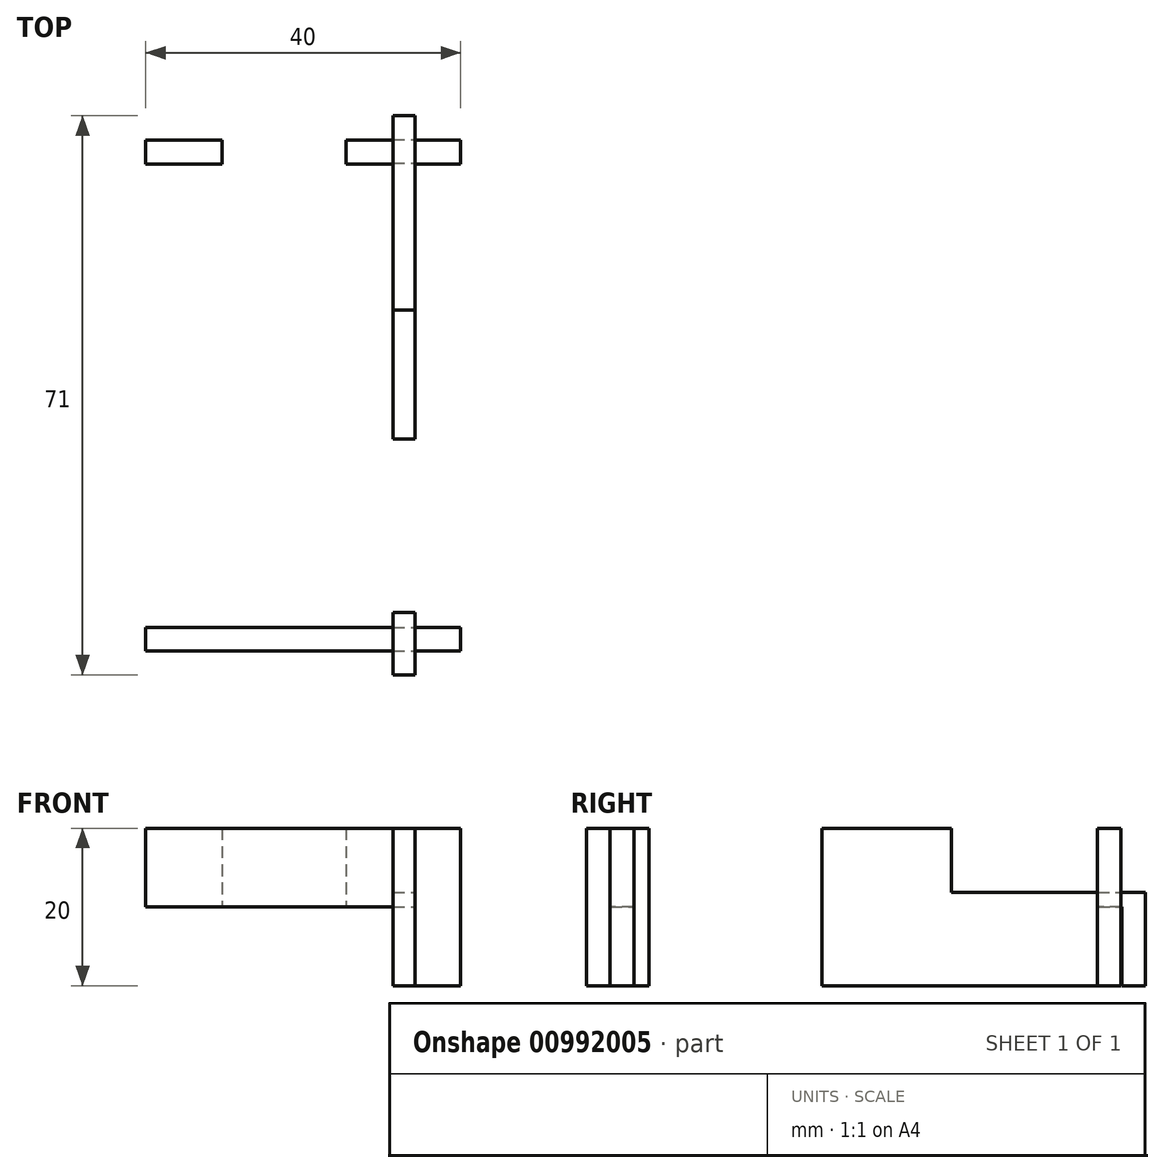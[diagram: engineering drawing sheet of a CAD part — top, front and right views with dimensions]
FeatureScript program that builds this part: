
annotation { "Feature Type Name" : "Feature", "Feature Type Description" : "" }
export const myFeature = defineFeature(function(context is Context, id is Id, definition is map)
    precondition{}
    {
        {
            var Q0;
            Q0=qCreatedBy(makeId("Front.planeOp"),FACE);
            var sketch = newSketch(context, id + "F0", { "sketchPlane" : qUnion([Q0])});
            skLineSegment(sketch, "E0.bottom", {"start": v(-40, 20) * mm, "end": v(0, 20) * mm});
            skLineSegment(sketch, "E0.top", {"start": v(-40, 0) * mm, "end": v(0, 0) * mm});
            skLineSegment(sketch, "E0.left", {"start": v(-40, 20) * mm, "end": v(-40, 0) * mm});
            skLineSegment(sketch, "E0.right", {"start": v(0, 20) * mm, "end": v(0, 0) * mm});
            skSolve(sketch);
        }
        {
            var Q0;
            Q0=makeQuery(id+"F0.imprint","IMPRINT",FACE,{"disambiguationData":[TD([[makeQuery(id+"F0.imprint","IMPRINT",EDGE,{"derivedFrom":sQuery(id+"F0.wireOp",EDGE,"E0.bottom")}),-1.0]])]});
            extrude(context, id + "F1", {"entities" : qUnion([Q0]), "depth" : 3 * mm, "offsetDistance" : 25 * mm});
        }
        {
            var Q0;
            Q0=makeQuery(id+"F1.opExtrude","SWEPT_FACE",FACE,{"disambiguationData":[OSD([sQuery(id+"F0.wireOp",EDGE,"E0.bottom")])]});
            var sketch = newSketch(context, id + "F2", { "sketchPlane" : qUnion([Q0])});
            skLineSegment(sketch, "E1.bottom", {"start": v(-8.59, 0) * mm, "end": v(-5.79, 0) * mm});
            skLineSegment(sketch, "E1.top", {"start": v(-8.59, -3) * mm, "end": v(-5.79, -3) * mm});
            skLineSegment(sketch, "E1.left", {"start": v(-8.59, 0) * mm, "end": v(-8.59, -3) * mm});
            skLineSegment(sketch, "E1.right", {"start": v(-5.79, 0) * mm, "end": v(-5.79, -3) * mm});
            skSolve(sketch);
        }
        {
            var Q0;
            Q0=makeQuery(id+"F2.imprint","IMPRINT",FACE,{"disambiguationData":[TD([[makeQuery(id+"F2.imprint","IMPRINT",EDGE,{"derivedFrom":sQuery(id+"F2.wireOp",EDGE,"E1.bottom")}),-1.0]])]});
            extrude(context, id + "F3", {"entities" : qUnion([Q0]), "operationType" : NewBodyOperationType.REMOVE, "oppositeDirection" : true, "depth" : 10 * mm, "offsetDistance" : 25 * mm});
        }
        {
            var Q0;
            {var subQ1=sQuery(id+"F0.wireOp",EDGE,"E0.left");var subQ3=sQuery(id+"F0.wireOp",EDGE,"E0.bottom");Q0=makeQuery(id+"F3.boolean.opBoolean","SPLIT",FACE,{"disambiguationData":[TD([makeQuery(id+"F1.opExtrude","SWEPT_FACE",FACE,{"disambiguationData":[OSD([subQ1])]})])],"derivedFrom":makeQuery(id+"F1.opExtrude","SWEPT_FACE",FACE,{"disambiguationData":[OSD([subQ3])]})});}
            var sketch = newSketch(context, id + "F4", { "sketchPlane" : qUnion([Q0])});
            skLineSegment(sketch, "E2", {"start": v(-8.59, 65) * mm, "end": v(-8.59, -6) * mm});
            skLineSegment(sketch, "E3", {"start": v(-8.59, -6) * mm, "end": v(-5.79, -6) * mm});
            skLineSegment(sketch, "E4", {"start": v(-5.79, -6) * mm, "end": v(-5.79, 65) * mm});
            skLineSegment(sketch, "E5", {"start": v(-5.79, 65) * mm, "end": v(-8.59, 65) * mm});
            skLineSegment(sketch, "E6", {"start": v(-14.6, 0) * mm, "end": v(-14.6, 59) * mm, "construction": true});
            skLineSegment(sketch, "E7", {"start": v(-14.6, 29.5) * mm, "end": v(-27.72, 29.5) * mm, "construction": true});
            skLineSegment(sketch, "E8", {"start": v(-8.59, 62) * mm, "end": v(-5.79, 62) * mm, "construction": true});
            skLineSegment(sketch, "E9", {"start": v(-8.59, -3) * mm, "end": v(-5.79, -3) * mm, "construction": true});
            skLineSegment(sketch, "E10", {"start": v(-7.19, -3) * mm, "end": v(-7.19, 62) * mm, "construction": true});
            skSolve(sketch);
        }
        {
            var Q0;
            {var subQ0=sQuery(id+"F4.wireOp",EDGE,"E3");Q0=makeQuery(id+"F4.imprint","IMPRINT",FACE,{"disambiguationData":[TD([[makeQuery(id+"F4.imprint","IMPRINT",EDGE,{"derivedFrom":subQ0}),1.0]])]});}
            var Q1;
            Q1=makeQuery(id+"F1.opExtrude","SWEPT_FACE",FACE,{"disambiguationData":[OSD([sQuery(id+"F0.wireOp",EDGE,"E0.top")])]});
            extrude(context, id + "F5", {"entities" : qUnion([Q0]), "endBound" : BoundingType.UP_TO_SURFACE, "oppositeDirection" : true, "depth" : 25 * mm, "endBoundEntityFace" : qUnion([Q1]), "offsetDistance" : 25 * mm});
        }
        {
            var Q0;
            {var subQ0=sQuery(id+"F4.wireOp",EDGE,"E5");var subQ1=sQuery(id+"F4.wireOp",EDGE,"E4");Q0=makeQuery(id+"F5.boolean.opBoolean","SPLIT",FACE,{"disambiguationData":[TD([makeQuery(id+"F5.opExtrude","SWEPT_FACE",FACE,{"disambiguationData":[OSD([subQ0])]})])],"derivedFrom":makeQuery(id+"F5.opExtrude","SWEPT_FACE",FACE,{"disambiguationData":[OSD([subQ1])]})});}
            var sketch = newSketch(context, id + "F6", { "sketchPlane" : qUnion([Q0])});
            skLineSegment(sketch, "E11", {"start": v(-3, 10) * mm, "end": v(-3, 0) * mm});
            skLineSegment(sketch, "E12", {"start": v(-3, 0) * mm, "end": v(0, 0) * mm});
            skLineSegment(sketch, "E13", {"start": v(0, 0) * mm, "end": v(0, 10) * mm});
            skLineSegment(sketch, "E14", {"start": v(0, 10) * mm, "end": v(-3, 10) * mm});
            skLineSegment(sketch, "E15.0", {"start": v(-6, 20) * mm, "end": v(65, 20) * mm, "construction": true});
            skLineSegment(sketch, "E16", {"start": v(29.5, 20) * mm, "end": v(29.5, -9.87) * mm, "construction": true});
            skLineSegment(sketch, "E17.MirrorCS", {"start": v(59, 10) * mm, "end": v(62, 10) * mm});
            skLineSegment(sketch, "E18.MirrorCS", {"start": v(59, 0) * mm, "end": v(59, 10) * mm});
            skLineSegment(sketch, "E19.MirrorCS", {"start": v(62, 10) * mm, "end": v(62, 0) * mm});
            skLineSegment(sketch, "E20.MirrorCS", {"start": v(62, 0) * mm, "end": v(59, 0) * mm});
            skSolve(sketch);
        }
        {
            var Q0;
            Q0 = qSketchRegion(id + "F6", true);
            extrude(context, id + "F7", {"entities" : qUnion([Q0]), "operationType" : NewBodyOperationType.REMOVE, "endBound" : BoundingType.THROUGH_ALL, "oppositeDirection" : true, "depth" : 25 * mm, "offsetDistance" : 25 * mm});
        }
        {
            var Q0;
            Q0=makeQuery(id+"F5.opExtrude","SWEPT_FACE",FACE,{"disambiguationData":[OSD([sQuery(id+"F4.wireOp",EDGE,"E4")])]});
            var sketch = newSketch(context, id + "F8", { "sketchPlane" : qUnion([Q0])});
            skLineSegment(sketch, "E21.bottom", {"start": v(1.92, 20) * mm, "end": v(23.92, 20) * mm});
            skLineSegment(sketch, "E21.top", {"start": v(1.92, 0) * mm, "end": v(23.92, 0) * mm});
            skLineSegment(sketch, "E21.left", {"start": v(1.92, 20) * mm, "end": v(1.92, 0) * mm});
            skLineSegment(sketch, "E21.right", {"start": v(23.92, 20) * mm, "end": v(23.92, 0) * mm});
            skSolve(sketch);
        }
        {
            var Q0;
            Q0=makeQuery(id+"F8.imprint","IMPRINT",FACE,{"disambiguationData":[TD([[makeQuery(id+"F8.imprint","IMPRINT",EDGE,{"derivedFrom":sQuery(id+"F8.wireOp",EDGE,"E21.bottom")}),-1.0]])]});
            extrude(context, id + "F9", {"entities" : qUnion([Q0]), "operationType" : NewBodyOperationType.REMOVE, "oppositeDirection" : true, "depth" : 25 * mm, "offsetDistance" : 25 * mm});
        }
        {
            var Q0;
            {var subQ0=sQuery(id+"F4.wireOp",EDGE,"E5");var subQ1=sQuery(id+"F4.wireOp",EDGE,"E4");Q0=makeQuery(id+"F9.boolean.opBoolean","SPLIT",FACE,{"disambiguationData":[TD([makeQuery(id+"F5.opExtrude","SWEPT_FACE",FACE,{"disambiguationData":[OSD([subQ0])]})])],"derivedFrom":makeQuery(id+"F5.opExtrude","SWEPT_FACE",FACE,{"disambiguationData":[OSD([subQ1])]})});}
            var sketch = newSketch(context, id + "F10", { "sketchPlane" : qUnion([Q0])});
            skLineSegment(sketch, "E22", {"start": v(40.33, 20) * mm, "end": v(40.33, 11.87) * mm});
            skLineSegment(sketch, "E23", {"start": v(40.33, 11.87) * mm, "end": v(65, 11.87) * mm});
            skLineSegment(sketch, "E24", {"start": v(40.33, 20) * mm, "end": v(65, 20) * mm});
            skLineSegment(sketch, "E25", {"start": v(65, 20) * mm, "end": v(65, 11.87) * mm});
            skSolve(sketch);
        }
        {
            var Q0;
            Q0=makeQuery(id+"F10.imprint","IMPRINT",FACE,{"disambiguationData":[TD([[makeQuery(id+"F10.imprint","IMPRINT",EDGE,{"derivedFrom":sQuery(id+"F10.wireOp",EDGE,"E22")}),1.0]])]});
            extrude(context, id + "F11", {"entities" : qUnion([Q0]), "operationType" : NewBodyOperationType.REMOVE, "oppositeDirection" : true, "depth" : 25 * mm, "offsetDistance" : 25 * mm});
        }
        {
            var Q0;
            Q0=makeQuery(id+"F1.opExtrude","SWEPT_BODY",BODY,{"disambiguationData":[OSD([sQuery(id+"F0.wireOp",EDGE,"E0.bottom"),sQuery(id+"F0.wireOp",EDGE,"E0.top"),sQuery(id+"F0.wireOp",EDGE,"E0.left"),sQuery(id+"F0.wireOp",EDGE,"E0.right")])]});
            transform(context, id + "F12", {"entities" : qUnion([Q0]), "transformType" : TransformType.TRANSLATION_3D, "dx" : 0 * mm, "dy" : 61.9 * mm, "dz" : 0 * mm, "makeCopy" : true});
        }
        {
            var Q0;
            Q0=makeQuery(id+"F12.opPattern","COPY",FACE,{"derivedFrom":makeQuery(id+"F1.opExtrude","CAP_FACE",FACE,{"disambiguationData":[OSD([sQuery(id+"F0.wireOp",EDGE,"E0.bottom"),sQuery(id+"F0.wireOp",EDGE,"E0.top"),sQuery(id+"F0.wireOp",EDGE,"E0.left"),sQuery(id+"F0.wireOp",EDGE,"E0.right")])],"isStart":true}),"instanceName":"1"});
            var sketch = newSketch(context, id + "F13", { "sketchPlane" : qUnion([Q0])});
            skLineSegment(sketch, "E26", {"start": v(14.56, 20) * mm, "end": v(14.56, 8.14) * mm});
            skLineSegment(sketch, "E27", {"start": v(14.56, 8.14) * mm, "end": v(30.32, 8.14) * mm});
            skLineSegment(sketch, "E28", {"start": v(30.32, 8.14) * mm, "end": v(30.32, 20) * mm});
            skLineSegment(sketch, "E29", {"start": v(30.32, 20) * mm, "end": v(14.56, 20) * mm});
            skSolve(sketch);
        }
        {
            var Q0;
            Q0=makeQuery(id+"F13.imprint","IMPRINT",FACE,{"disambiguationData":[TD([[makeQuery(id+"F13.imprint","IMPRINT",EDGE,{"derivedFrom":sQuery(id+"F13.wireOp",EDGE,"E26")}),1.0]])]});
            extrude(context, id + "F14", {"entities" : qUnion([Q0]), "operationType" : NewBodyOperationType.REMOVE, "oppositeDirection" : true, "depth" : 25 * mm, "offsetDistance" : 25 * mm});
        }
    });
